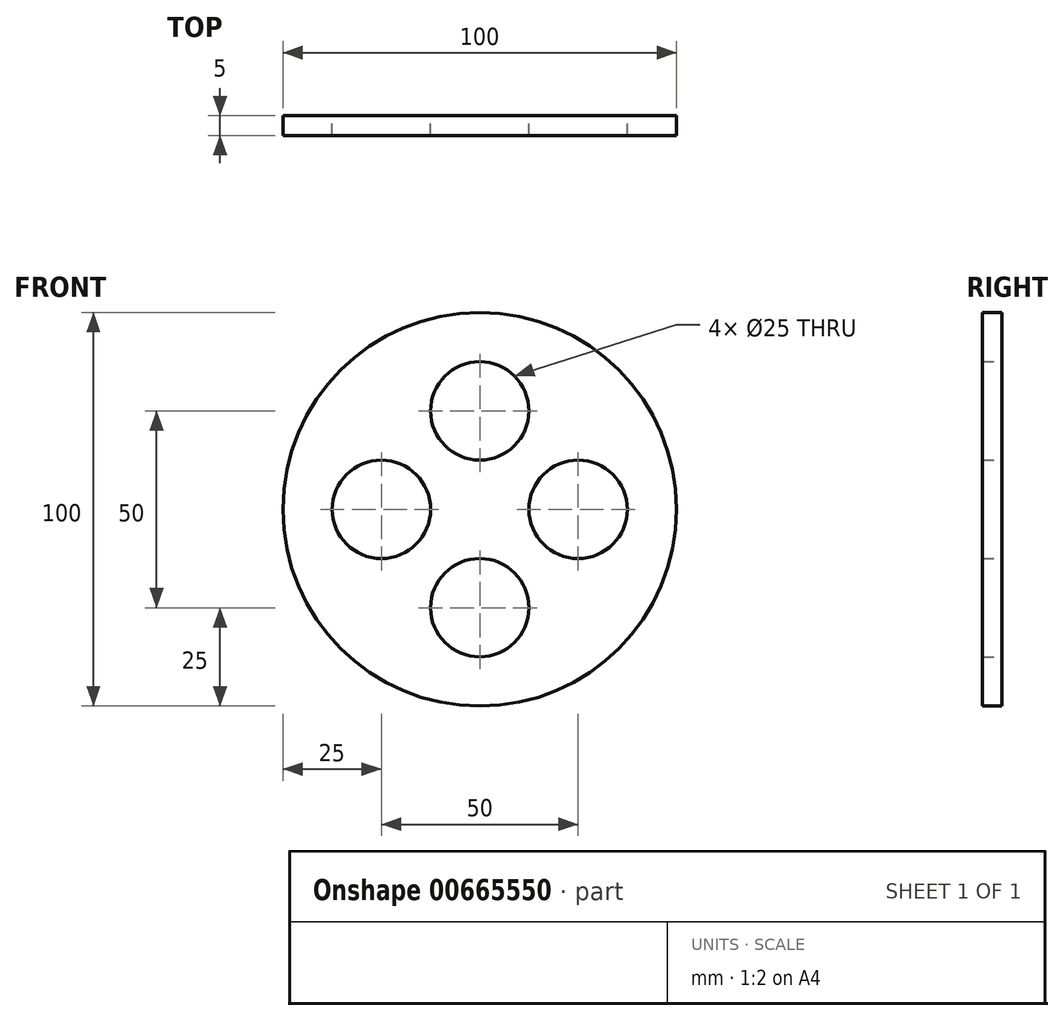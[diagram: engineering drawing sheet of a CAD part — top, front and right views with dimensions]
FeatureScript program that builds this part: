
annotation { "Feature Type Name" : "Feature", "Feature Type Description" : "" }
export const myFeature = defineFeature(function(context is Context, id is Id, definition is map)
    precondition{}
    {
        {
            var Q0;
            Q0=qCreatedBy(makeId("Front.planeOp"),FACE);
            var sketch = newSketch(context, id + "F0", { "sketchPlane" : qUnion([Q0])});
            skCircle(sketch, "E0", {"center": v(0, 0) * mm, "radius": 50 * mm});
            skLineSegment(sketch, "E1", {"start": v(0, 0) * mm, "end": v(50, 0) * mm});
            skCircle(sketch, "E2", {"center": v(25, 0) * mm, "radius": 12.5 * mm});
            skCircle(sketch, "E3.1.0", {"center": v(0, 25) * mm, "radius": 12.5 * mm});
            skCircle(sketch, "E3.2.0", {"center": v(-25, 0) * mm, "radius": 12.5 * mm});
            skCircle(sketch, "E3.3.0", {"center": v(0, -25) * mm, "radius": 12.5 * mm});
            skSolve(sketch);
        }
        {
            var Q0;
            Q0=makeQuery(id+"F0.imprint","IMPRINT",FACE,{"disambiguationData":[TD([[makeQuery(id+"F0.imprint","IMPRINT",EDGE,{"derivedFrom":sQuery(id+"F0.wireOp",EDGE,"E0")}),1.0]])]});
            extrude(context, id + "F1", {"entities" : qUnion([Q0]), "depth" : 5 * mm, "offsetDistance" : 25 * mm});
        }
    });
